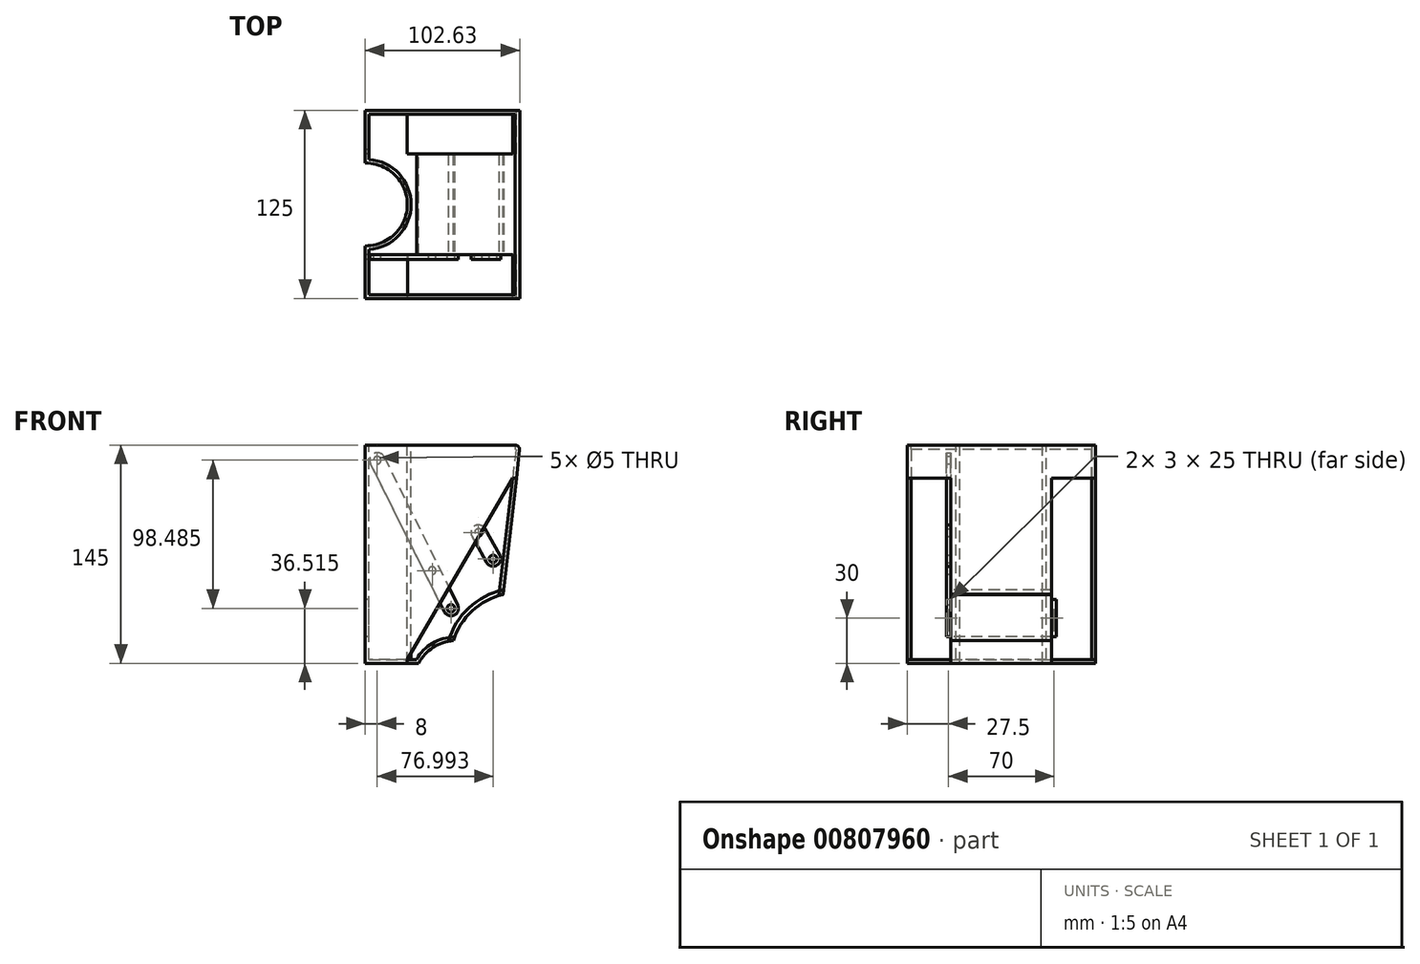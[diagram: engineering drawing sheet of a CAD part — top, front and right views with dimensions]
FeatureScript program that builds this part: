
annotation { "Feature Type Name" : "Feature", "Feature Type Description" : "" }
export const myFeature = defineFeature(function(context is Context, id is Id, definition is map)
    precondition{}
    {
        {
            var Q0;
            Q0=qCreatedBy(makeId("Front.planeOp"),FACE);
            var sketch = newSketch(context, id + "F0", { "sketchPlane" : qUnion([Q0])});
            skLineSegment(sketch, "E0", {"start": v(0, 130) * mm, "end": v(75, 130) * mm});
            skArc(sketch, "E1", {"start": v(56.58, -15) * mm, "mid": v(32.08, 0) * mm, "end": v(7.59, -15) * mm});
            skLineSegment(sketch, "E2", {"start": v(0, -15) * mm, "end": v(7.59, -15) * mm});
            skLineSegment(sketch, "E3.trimOffspring", {"start": v(56.58, -15) * mm, "end": v(58.27, -15) * mm});
            skLineSegment(sketch, "E4", {"start": v(75, 130) * mm, "end": v(58.27, -15) * mm});
            skLineSegment(sketch, "E5", {"start": v(0, 130) * mm, "end": v(-28, 130) * mm});
            skLineSegment(sketch, "E6", {"start": v(0, -15) * mm, "end": v(-28, -15) * mm});
            skLineSegment(sketch, "E7", {"start": v(-28, -15) * mm, "end": v(-28, 130) * mm});
            skLineSegment(sketch, "E8", {"start": v(75.45, 0) * mm, "end": v(-49.86, 0) * mm, "construction": true});
            skLineSegment(sketch, "E9", {"start": v(0, -37.66) * mm, "end": v(0, 158.2) * mm, "construction": true});
            skSolve(sketch);
        }
        {
            var Q0;
            Q0=makeQuery(id+"F0.imprint","IMPRINT",FACE,{"disambiguationData":[TD([[makeQuery(id+"F0.imprint","IMPRINT",EDGE,{"derivedFrom":sQuery(id+"F0.wireOp",EDGE,"AEWyvxpA-VYwD-7hNY-brtb-rKHveOHAXlaS")}),-1.0]])]});
            var Q1;
            Q1=makeQuery(id+"F0.imprint","IMPRINT",FACE,{"disambiguationData":[TD([[makeQuery(id+"F0.imprint","IMPRINT",EDGE,{"derivedFrom":sQuery(id+"F0.wireOp",EDGE,"E0")}),-1.0]])]});
            extrude(context, id + "F1", {"entities" : qUnion([Q0, Q1]), "depth" : 125 * mm, "offsetDistance" : 25 * mm});
        }
        {
            var Q0;
            Q0=makeQuery(id+"F1.opExtrude","SWEPT_FACE",FACE,{"disambiguationData":[OSD([sQuery(id+"F0.wireOp",EDGE,"E0"),sQuery(id+"F0.wireOp",EDGE,"E5")])]});
            cPlane(context, id + "F2", {"entities" : qUnion([Q0]), "cplaneType" : CPlaneType.OFFSET, "offset" : 0 * mm, "width" : 150 * mm, "height" : 150 * mm});
        }
        {
            var Q0;
            Q0=qCreatedBy(id+"F2.planeOp",FACE);
            var sketch = newSketch(context, id + "F3", { "sketchPlane" : qUnion([Q0])});
            skCircle(sketch, "E10", {"center": v(-27.5, -62.5) * mm, "radius": 27.5 * mm});
            skLineSegment(sketch, "E11", {"start": v(0, 0) * mm, "end": v(0, -125) * mm, "construction": true});
            skLineSegment(sketch, "E12", {"start": v(0, 0) * mm, "end": v(0, -62.5) * mm, "construction": true});
            skSolve(sketch);
        }
        {
            var Q0;
            Q0=makeQuery(id+"F3.imprint","IMPRINT",FACE,{"disambiguationData":[TD([[makeQuery(id+"F3.imprint","IMPRINT",EDGE,{"derivedFrom":sQuery(id+"F3.wireOp",EDGE,"E10")}),1.0]])]});
            extrude(context, id + "F4", {"entities" : qUnion([Q0]), "operationType" : NewBodyOperationType.REMOVE, "oppositeDirection" : true, "depth" : 171.8 * mm, "offsetDistance" : 25 * mm});
        }
        {
            var Q0;
            Q0=makeQuery(id+"F1.opExtrude","SWEPT_EDGE",EDGE,{"disambiguationData":[OSD([sQuery(id+"F0.wireOp",EDGE,"E0"),sQuery(id+"F0.wireOp",EDGE,"E4")])]});
            fillet(context, id + "F5", {"entities" : qUnion([Q0]), "radius" : 3 * mm, "tangentPropagation" : true, "allowEdgeOverflow" : false});
        }
        {
            var Q0;
            Q0=makeQuery(id+"F1.opExtrude","SWEPT_FACE",FACE,{"disambiguationData":[OSD([sQuery(id+"F0.wireOp",EDGE,"E0"),sQuery(id+"F0.wireOp",EDGE,"E5")])]});
            shell(context, id + "F6", {"entities" : qUnion([Q0]), "thickness" : 2.5 * mm});
        }
        {
            var Q0;
            {var subQ0=sQuery(id+"F0.wireOp",EDGE,"E7");var subQ1=sQuery(id+"F0.wireOp",EDGE,"E6");var subQ2=sQuery(id+"F0.wireOp",EDGE,"E5");var subQ3=sQuery(id+"F0.wireOp",EDGE,"E2");var subQ4=sQuery(id+"F0.wireOp",EDGE,"E0");Q0=makeQuery(id+"F4.boolean.opBoolean","SPLIT",FACE,{"disambiguationData":[TD([makeQuery(id+"F1.opExtrude","CAP_FACE",FACE,{"disambiguationData":[OSD([subQ4,sQuery(id+"F0.wireOp",EDGE,"E1"),subQ3,sQuery(id+"F0.wireOp",EDGE,"E3.trimOffspring"),sQuery(id+"F0.wireOp",EDGE,"E4"),subQ2,subQ1,subQ0])],"isStart":true})])],"derivedFrom":makeQuery(id+"F1.opExtrude","SWEPT_FACE",FACE,{"disambiguationData":[OSD([subQ0])]})});}
            cPlane(context, id + "F7", {"entities" : qUnion([Q0]), "cplaneType" : CPlaneType.OFFSET, "offset" : 0 * mm, "width" : 150 * mm, "height" : 150 * mm});
        }
        {
            var Q0;
            Q0=qCreatedBy(id+"F7.planeOp",FACE);
            var sketch = newSketch(context, id + "F8", { "sketchPlane" : qUnion([Q0])});
            skLineSegment(sketch, "E13.bottom", {"start": v(29, 2.5) * mm, "end": v(26, 2.5) * mm});
            skLineSegment(sketch, "E13.top", {"start": v(29, 27.5) * mm, "end": v(26, 27.5) * mm});
            skLineSegment(sketch, "E13.left", {"start": v(29, 2.5) * mm, "end": v(29, 27.5) * mm});
            skLineSegment(sketch, "E13.right", {"start": v(26, 2.5) * mm, "end": v(26, 27.5) * mm});
            skLineSegment(sketch, "E14.bottom", {"start": v(96, 2.5) * mm, "end": v(99, 2.5) * mm});
            skLineSegment(sketch, "E14.top", {"start": v(96, 27.5) * mm, "end": v(99, 27.5) * mm});
            skLineSegment(sketch, "E14.left", {"start": v(96, 2.5) * mm, "end": v(96, 27.5) * mm});
            skLineSegment(sketch, "E14.right", {"start": v(99, 2.5) * mm, "end": v(99, 27.5) * mm});
            skLineSegment(sketch, "E15.bottom", {"start": v(99, 2.5) * mm, "end": v(96, 2.5) * mm});
            skSolve(sketch);
        }
        {
            var Q0;
            Q0=makeQuery(id+"F8.imprint","IMPRINT",FACE,{"disambiguationData":[TD([[makeQuery(id+"F8.imprint","IMPRINT",EDGE,{"derivedFrom":sQuery(id+"F8.wireOp",EDGE,"E13.bottom")}),-1.0]])]});
            var Q1;
            Q1=makeQuery(id+"F8.imprint","IMPRINT",FACE,{"disambiguationData":[TD([[makeQuery(id+"F8.imprint","IMPRINT",EDGE,{"derivedFrom":sQuery(id+"F8.wireOp",EDGE,"E14.top")}),-1.0]])]});
            extrude(context, id + "F9", {"entities" : qUnion([Q0, Q1]), "operationType" : NewBodyOperationType.REMOVE, "oppositeDirection" : true, "depth" : 35.1 * mm, "offsetDistance" : 25 * mm});
        }
        {
            var Q0;
            Q0=qCreatedBy(id+"F7.planeOp",FACE);
            cPlane(context, id + "F10", {"entities" : qUnion([Q0]), "cplaneType" : CPlaneType.OFFSET, "offset" : 110 * mm, "oppositeDirection" : true, "width" : 150 * mm, "height" : 150 * mm});
        }
        {
            var Q0;
            Q0=qCreatedBy(id+"F10.planeOp",FACE);
            var sketch = newSketch(context, id + "F11", { "sketchPlane" : qUnion([Q0])});
            skLineSegment(sketch, "E16.bottom", {"start": v(102, -15) * mm, "end": v(99, -15) * mm});
            skLineSegment(sketch, "E16.top", {"start": v(102, 108) * mm, "end": v(99, 108) * mm});
            skLineSegment(sketch, "E16.left", {"start": v(102, -15) * mm, "end": v(102, 108) * mm});
            skLineSegment(sketch, "E16.right", {"start": v(99, -15) * mm, "end": v(99, 108) * mm});
            skLineSegment(sketch, "E17.bottom", {"start": v(26, -15) * mm, "end": v(23, -15) * mm});
            skLineSegment(sketch, "E17.top", {"start": v(26, 108) * mm, "end": v(23, 108) * mm});
            skLineSegment(sketch, "E17.left", {"start": v(26, -15) * mm, "end": v(26, 108) * mm});
            skLineSegment(sketch, "E17.right", {"start": v(23, -15) * mm, "end": v(23, 108) * mm});
            skSolve(sketch);
        }
        {
            var Q0;
            Q0=makeQuery(id+"F11.imprint","IMPRINT",FACE,{"disambiguationData":[TD([[makeQuery(id+"F11.imprint","IMPRINT",EDGE,{"derivedFrom":sQuery(id+"F11.wireOp",EDGE,"E16.bottom")}),-1.0]])]});
            var Q1;
            Q1=makeQuery(id+"F11.imprint","IMPRINT",FACE,{"disambiguationData":[TD([[makeQuery(id+"F11.imprint","IMPRINT",EDGE,{"derivedFrom":sQuery(id+"F11.wireOp",EDGE,"E17.bottom")}),-1.0]])]});
            extrude(context, id + "F12", {"entities" : qUnion([Q0, Q1]), "operationType" : NewBodyOperationType.REMOVE, "depth" : 23.73 * mm, "offsetDistance" : 25 * mm});
        }
        {
            var Q0;
            Q0=makeQuery(id+"F1.opExtrude","SWEPT_FACE",FACE,{"disambiguationData":[OSD([sQuery(id+"F0.wireOp",EDGE,"E2"),sQuery(id+"F0.wireOp",EDGE,"E6")])]});
            cPlane(context, id + "F13", {"entities" : qUnion([Q0]), "cplaneType" : CPlaneType.OFFSET, "offset" : 0 * mm, "width" : 150 * mm, "height" : 150 * mm});
        }
        {
            var Q0;
            Q0=makeQuery(id+"F1.opExtrude","CAP_FACE",FACE,{"disambiguationData":[OSD([sQuery(id+"F0.wireOp",EDGE,"E0"),sQuery(id+"F0.wireOp",EDGE,"E1"),sQuery(id+"F0.wireOp",EDGE,"E2"),sQuery(id+"F0.wireOp",EDGE,"E3.trimOffspring"),sQuery(id+"F0.wireOp",EDGE,"E4"),sQuery(id+"F0.wireOp",EDGE,"E5"),sQuery(id+"F0.wireOp",EDGE,"E6"),sQuery(id+"F0.wireOp",EDGE,"E7")])],"isStart":false});
            cPlane(context, id + "F14", {"entities" : qUnion([Q0]), "cplaneType" : CPlaneType.OFFSET, "offset" : 29 * mm, "oppositeDirection" : true, "width" : 150 * mm, "height" : 150 * mm});
        }
        {
            var Q0;
            Q0=qCreatedBy(id+"F14.planeOp",FACE);
            var sketch = newSketch(context, id + "F15", { "sketchPlane" : qUnion([Q0])});
            skCircle(sketch, "E18", {"center": v(73.93, -13.54) * mm, "radius": 45.5 * mm});
            skSolve(sketch);
        }
        {
            var Q0;
            Q0=makeQuery(id+"F15.imprint","IMPRINT",FACE,{"disambiguationData":[TD([[makeQuery(id+"F15.imprint","IMPRINT",EDGE,{"derivedFrom":sQuery(id+"F15.wireOp",EDGE,"E18")}),1.0]])]});
            var Q1;
            Q1=sQuery(id+"F15.wireOp",EDGE,"E18");
            extrude(context, id + "F16", {"entities" : qUnion([Q0]), "operationType" : NewBodyOperationType.REMOVE, "surfaceEntities" : qUnion([Q1]), "oppositeDirection" : true, "depth" : 70 * mm, "offsetDistance" : 25 * mm});
        }
        {
            var Q0;
            Q0=qCreatedBy(id+"F14.planeOp",FACE);
            var sketch = newSketch(context, id + "F17", { "sketchPlane" : qUnion([Q0])});
            skArc(sketch, "E19", {"start": v(63.52, 30.66) * mm, "mid": v(43, 19.72) * mm, "end": v(30.56, 0.06) * mm});
            skArc(sketch, "E20", {"start": v(63.89, 33.82) * mm, "mid": v(40.86, 21.83) * mm, "end": v(27.32, -0.31) * mm});
            skArc(sketch, "E21", {"start": v(30.56, 0.06) * mm, "mid": v(28.93, -0.08) * mm, "end": v(27.32, -0.31) * mm});
            skLineSegment(sketch, "E22", {"start": v(63.52, 30.66) * mm, "end": v(63.89, 33.82) * mm});
            skLineSegment(sketch, "E23", {"start": v(63.89, 33.82) * mm, "end": v(63.52, 30.66) * mm});
            skSolve(sketch);
        }
        {
            var Q0;
            Q0=qSketchRegion(id+"F17",true);
            extrude(context, id + "F18", {"entities" : qUnion([Q0]), "oppositeDirection" : true, "depth" : 70 * mm, "offsetDistance" : 25 * mm});
        }
        {
            var Q0;
            Q0=qCreatedBy(id+"F14.planeOp",FACE);
            var sketch = newSketch(context, id + "F19", { "sketchPlane" : qUnion([Q0])});
            skLineSegment(sketch, "E24", {"start": v(0, -12.59) * mm, "end": v(0, -15.04) * mm});
            skLineSegment(sketch, "E25", {"start": v(0, -15.04) * mm, "end": v(58.34, -15.04) * mm});
            skLineSegment(sketch, "E26", {"start": v(58.34, -15.04) * mm, "end": v(72.46, 108) * mm});
            skLineSegment(sketch, "E27", {"start": v(69.95, 108) * mm, "end": v(0, -12.59) * mm});
            skLineSegment(sketch, "E28", {"start": v(69.95, 108) * mm, "end": v(72.46, 108) * mm});
            skSolve(sketch);
        }
        {
            var Q0;
            Q0=makeQuery(id+"F19.imprint","IMPRINT",FACE,{"disambiguationData":[TD([[makeQuery(id+"F19.imprint","IMPRINT",EDGE,{"derivedFrom":sQuery(id+"F19.wireOp",EDGE,"E24")}),1.0]])]});
            extrude(context, id + "F20", {"entities" : qUnion([Q0]), "operationType" : NewBodyOperationType.REMOVE, "depth" : 47.2 * mm, "offsetDistance" : 25 * mm});
        }
        {
            var Q0;
            Q0=makeQuery(id+"F1.opExtrude","CAP_FACE",FACE,{"disambiguationData":[OSD([sQuery(id+"F0.wireOp",EDGE,"E0"),sQuery(id+"F0.wireOp",EDGE,"E1"),sQuery(id+"F0.wireOp",EDGE,"E2"),sQuery(id+"F0.wireOp",EDGE,"E3.trimOffspring"),sQuery(id+"F0.wireOp",EDGE,"E4"),sQuery(id+"F0.wireOp",EDGE,"E5"),sQuery(id+"F0.wireOp",EDGE,"E6"),sQuery(id+"F0.wireOp",EDGE,"E7")])],"isStart":true});
            var sketch = newSketch(context, id + "F21", { "sketchPlane" : qUnion([Q0])});
            skLineSegment(sketch, "E29", {"start": v(-72.46, 108.01) * mm, "end": v(-69.95, 108.01) * mm});
            skLineSegment(sketch, "E30", {"start": v(-69.95, 108.01) * mm, "end": v(0, -12.5) * mm});
            skLineSegment(sketch, "E31", {"start": v(0, -12.5) * mm, "end": v(0, -15) * mm});
            skLineSegment(sketch, "E32", {"start": v(0, -15) * mm, "end": v(-58.27, -15) * mm});
            skLineSegment(sketch, "E33", {"start": v(-58.27, -15) * mm, "end": v(-72.46, 108.01) * mm});
            skSolve(sketch);
        }
        {
            var Q0;
            Q0=makeQuery(id+"F21.imprint","IMPRINT",FACE,{"disambiguationData":[TD([[makeQuery(id+"F21.imprint","IMPRINT",EDGE,{"derivedFrom":sQuery(id+"F21.wireOp",EDGE,"E29")}),-1.0]])]});
            extrude(context, id + "F22", {"entities" : qUnion([Q0]), "operationType" : NewBodyOperationType.REMOVE, "oppositeDirection" : true, "depth" : 29 * mm, "offsetDistance" : 25 * mm});
        }
        {
            var Q0;
            Q0=qCreatedBy(id+"F14.planeOp",FACE);
            var sketch = newSketch(context, id + "F23", { "sketchPlane" : qUnion([Q0])});
            skArc(sketch, "E34", {"start": v(-15.52, 122.23) * mm, "mid": v(-22.23, 124.48) * mm, "end": v(-24.48, 117.77) * mm});
            skArc(sketch, "E35", {"start": v(24.52, 19.29) * mm, "mid": v(31.22, 17.04) * mm, "end": v(33.47, 23.74) * mm});
            skLineSegment(sketch, "E36", {"start": v(24.52, 19.29) * mm, "end": v(-24.48, 117.77) * mm});
            skCircle(sketch, "E37", {"center": v(-20, 120) * mm, "radius": 2.5 * mm});
            skCircle(sketch, "E38", {"center": v(29, 21.51) * mm, "radius": 2.5 * mm});
            skCircle(sketch, "E39", {"center": v(16.52, 46.58) * mm, "radius": 2.5 * mm});
            skLineSegment(sketch, "E40", {"start": v(-15.52, 122.23) * mm, "end": v(33.47, 23.74) * mm});
            skArc(sketch, "E41", {"start": v(77.88, 91.62) * mm, "mid": v(70.84, 92.51) * mm, "end": v(70, 85.47) * mm});
            skCircle(sketch, "E42", {"center": v(73.92, 88.57) * mm, "radius": 2.5 * mm});
            skArc(sketch, "E43", {"start": v(82.16, 69.68) * mm, "mid": v(89.17, 68.77) * mm, "end": v(90.08, 75.78) * mm});
            skCircle(sketch, "E44", {"center": v(86.12, 72.73) * mm, "radius": 2.5 * mm});
            skLineSegment(sketch, "E45", {"start": v(77.88, 91.62) * mm, "end": v(90.08, 75.78) * mm});
            skLineSegment(sketch, "E46", {"start": v(70, 85.47) * mm, "end": v(82.16, 69.68) * mm});
            skSolve(sketch);
        }
        {
            var Q0;
            {var subQ0=sQuery(id+"F23.wireOp",EDGE,"CEpgBrpP-yiiY-twuG-gih4-8btHfCE1UIKM");Q0=makeQuery(id+"F23.imprint","IMPRINT",FACE,{"disambiguationData":[TD([[makeQuery(id+"F23.imprint","IMPRINT",EDGE,{"derivedFrom":subQ0}),-1.0]])]});}
            var Q1;
            Q1=makeQuery(id+"F23.imprint","IMPRINT",FACE,{"disambiguationData":[TD([[makeQuery(id+"F23.imprint","IMPRINT",EDGE,{"derivedFrom":sQuery(id+"F23.wireOp",EDGE,"E38")}),-1.0]])]});
            var Q2;
            Q2=makeQuery(id+"F23.imprint","IMPRINT",FACE,{"disambiguationData":[TD([[makeQuery(id+"F23.imprint","IMPRINT",EDGE,{"derivedFrom":sQuery(id+"F23.wireOp",EDGE,"E37")}),-1.0]])]});
            extrude(context, id + "F24", {"entities" : qUnion([Q0, Q1, Q2]), "depth" : 3 * mm, "offsetDistance" : 25 * mm});
        }
        {
            var Q0;
            Q0=qCreatedBy(id+"F14.planeOp",FACE);
            var sketch = newSketch(context, id + "F25", { "sketchPlane" : qUnion([Q0])});
            skArc(sketch, "E47", {"start": v(51.65, 74.35) * mm, "mid": v(44.85, 76.3) * mm, "end": v(42.9, 69.5) * mm});
            skCircle(sketch, "E48", {"center": v(47.28, 71.92) * mm, "radius": 2.5 * mm});
            skArc(sketch, "E49", {"start": v(52.62, 52.01) * mm, "mid": v(59.42, 50.07) * mm, "end": v(61.36, 56.87) * mm});
            skCircle(sketch, "E50", {"center": v(57, 54.44) * mm, "radius": 2.5 * mm});
            skLineSegment(sketch, "E51", {"start": v(51.65, 74.35) * mm, "end": v(61.36, 56.87) * mm});
            skLineSegment(sketch, "E52", {"start": v(52.62, 52.01) * mm, "end": v(42.9, 69.5) * mm});
            skSolve(sketch);
        }
        {
            var Q0;
            Q0=makeQuery(id+"F25.imprint","IMPRINT",FACE,{"disambiguationData":[TD([[makeQuery(id+"F25.imprint","IMPRINT",EDGE,{"derivedFrom":sQuery(id+"F25.wireOp",EDGE,"E47")}),1.0]])]});
            extrude(context, id + "F26", {"entities" : qUnion([Q0]), "depth" : 3 * mm, "offsetDistance" : 25 * mm});
        }
    });
